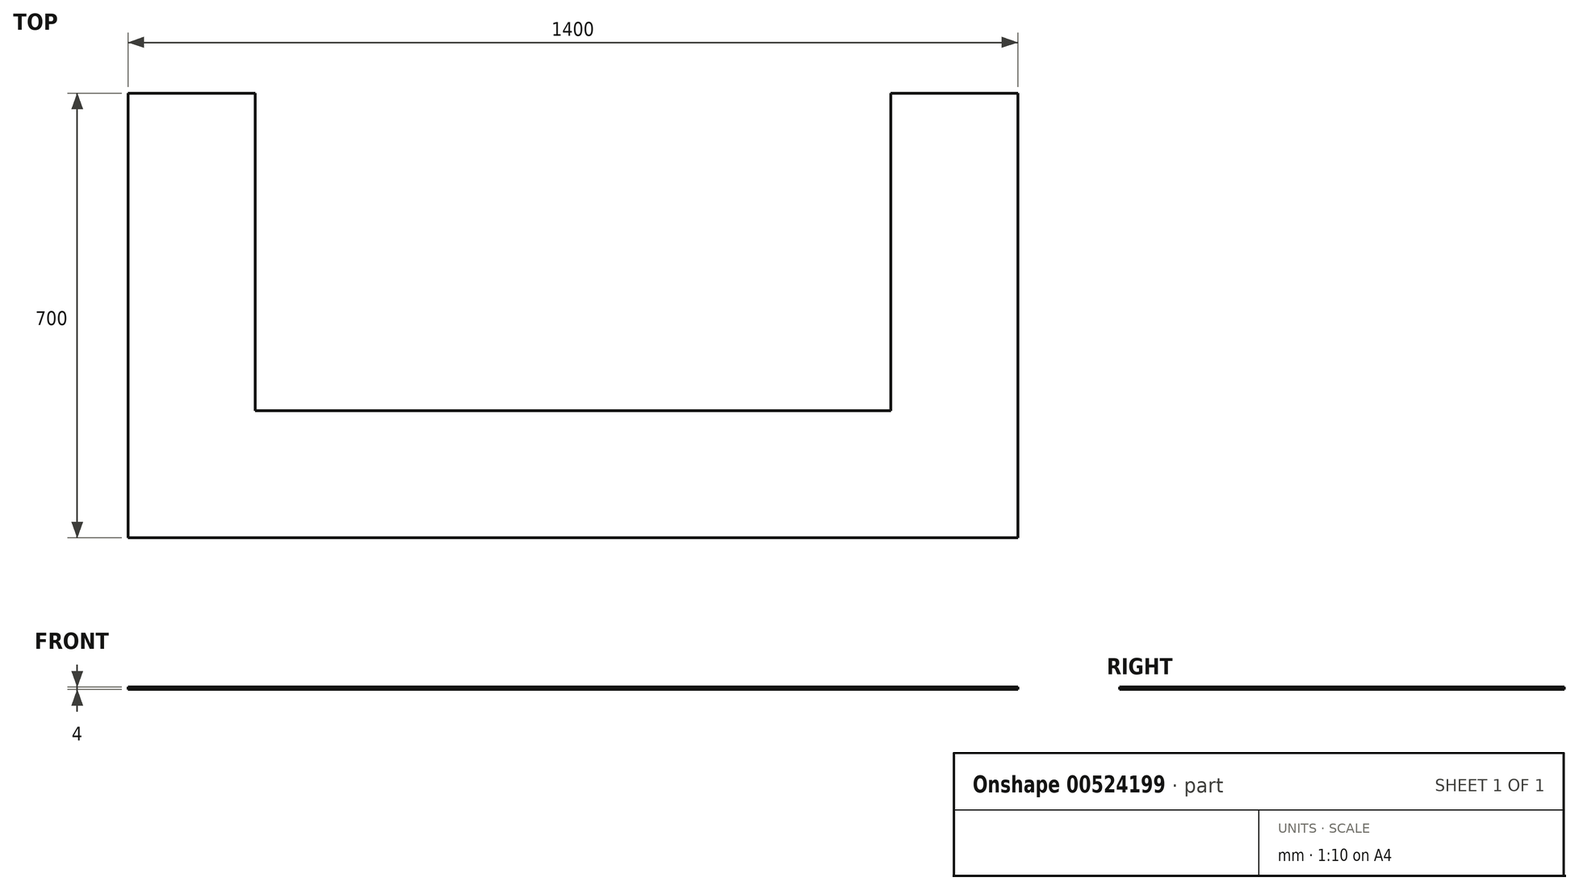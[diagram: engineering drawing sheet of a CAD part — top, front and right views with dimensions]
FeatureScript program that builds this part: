
annotation { "Feature Type Name" : "Feature", "Feature Type Description" : "" }
export const myFeature = defineFeature(function(context is Context, id is Id, definition is map)
    precondition{}
    {
        {
            var Q0;
            Q0=qCreatedBy(makeId("Top.planeOp"),FACE);
            var sketch = newSketch(context, id + "F0", { "sketchPlane" : qUnion([Q0])});
            skLineSegment(sketch, "E0.bottom", {"start": v(0, 0) * mm, "end": v(-1000, 0) * mm});
            skLineSegment(sketch, "E0.left", {"start": v(0, 0) * mm, "end": v(0, 500) * mm});
            skLineSegment(sketch, "E0.right", {"start": v(-1000, 0) * mm, "end": v(-1000, 500) * mm});
            skLineSegment(sketch, "E1.bottom", {"start": v(-1200, 500) * mm, "end": v(-1000, 500) * mm});
            skLineSegment(sketch, "E1.top", {"start": v(-1200, -200) * mm, "end": v(200, -200) * mm});
            skLineSegment(sketch, "E1.left", {"start": v(-1200, 500) * mm, "end": v(-1200, -200) * mm});
            skLineSegment(sketch, "E1.right", {"start": v(200, 500) * mm, "end": v(200, -200) * mm});
            skLineSegment(sketch, "E2.trimOffspring", {"start": v(0, 500) * mm, "end": v(200, 500) * mm});
            skSolve(sketch);
        }
        {
            var Q0;
            Q0 = qSketchRegion(id + "F0", true);
            extrude(context, id + "F1", {"entities" : qUnion([Q0]), "depth" : 4 * mm, "offsetDistance" : 25 * mm});
        }
    });
